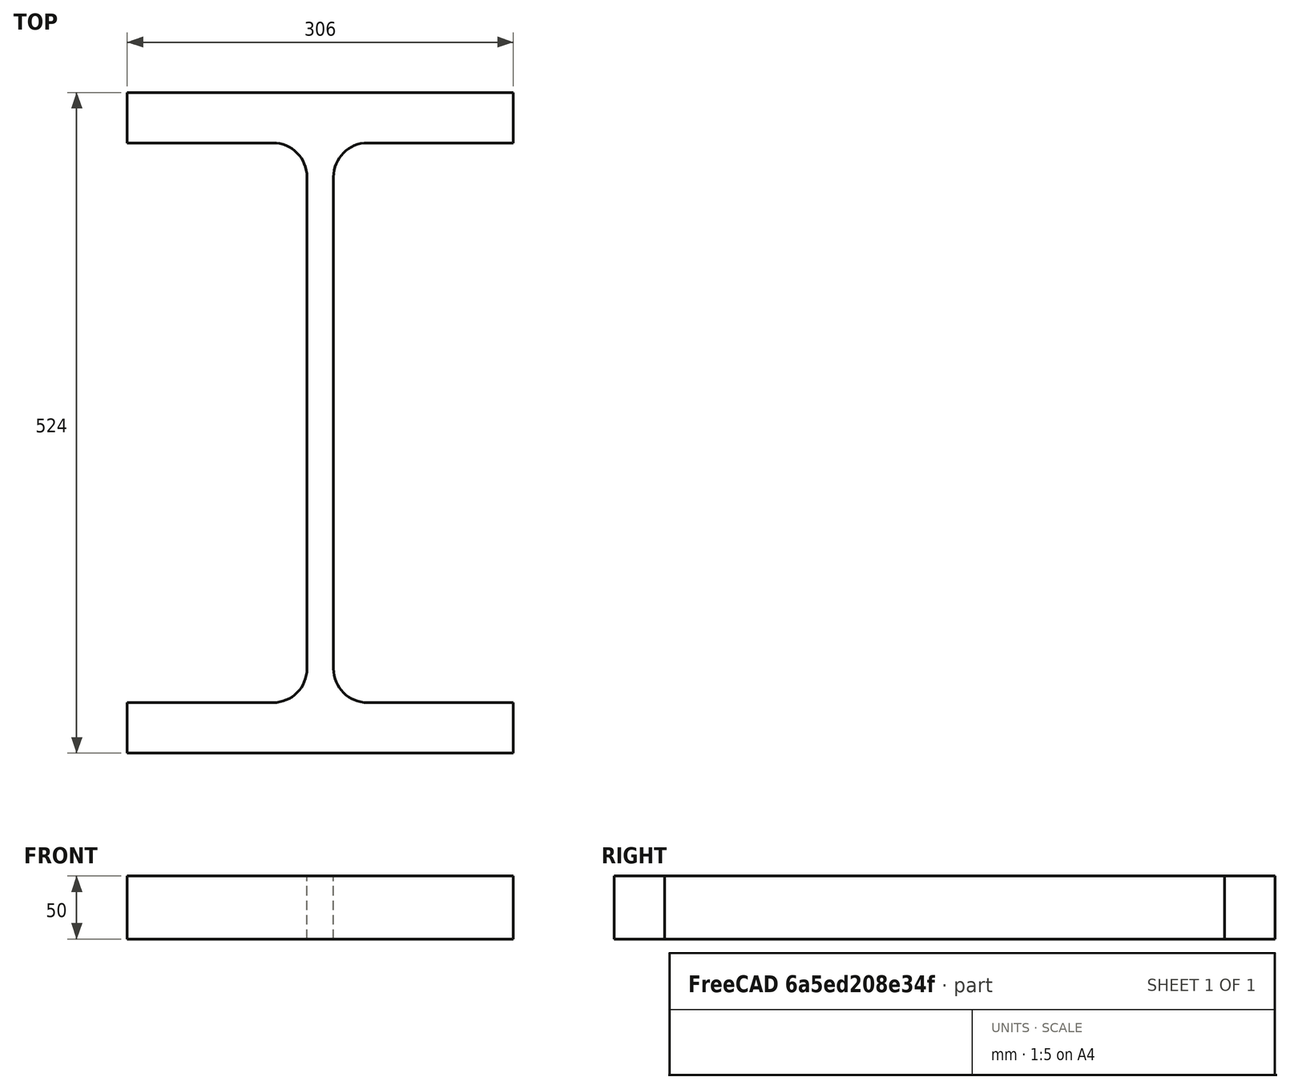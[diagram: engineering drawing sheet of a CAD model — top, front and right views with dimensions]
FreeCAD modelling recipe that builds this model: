
FCSTD DOCUMENT  (FreeCAD 0.15R4671 (Git))
Label: HE-M-Profile 500 DIN1025-4 S235JR
License: All rights reserved
LicenseURL: http://en.wikipedia.org/wiki/All_rights_reserved
objects: Sketcher::SketchObject×1, Part::Extrusion×1
note: 2 computed .brp shape members not serialized (recipe doc carries the construction recipe); baked Part::Feature solids carry a one-line shape summary decoded from their .brp

FEATURE [Sketcher::SketchObject] Sketch
  sketch-geometry (16):
    g0: LineSegment StartX=10.5 StartY=-195 StartZ=0 EndX=10.5 EndY=195 EndZ=0
    g1: LineSegment StartX=37.5 StartY=222 StartZ=0 EndX=153 EndY=222 EndZ=0
    g2: LineSegment StartX=153 StartY=222 StartZ=0 EndX=153 EndY=262 EndZ=0
    g3: LineSegment StartX=153 StartY=262 StartZ=0 EndX=-153 EndY=262 EndZ=0
    g4: LineSegment StartX=-153 StartY=262 StartZ=0 EndX=-153 EndY=222 EndZ=0
    g5: LineSegment StartX=-153 StartY=222 StartZ=0 EndX=-37.5 EndY=222 EndZ=0
    g6: LineSegment StartX=-10.5 StartY=195 StartZ=0 EndX=-10.5 EndY=-195 EndZ=0
    g7: LineSegment StartX=-37.5 StartY=-222 StartZ=0 EndX=-153 EndY=-222 EndZ=0
    g8: LineSegment StartX=-153 StartY=-222 StartZ=0 EndX=-153 EndY=-262 EndZ=0
    g9: LineSegment StartX=-153 StartY=-262 StartZ=0 EndX=153 EndY=-262 EndZ=0
    g10: LineSegment StartX=153 StartY=-262 StartZ=0 EndX=153 EndY=-222 EndZ=0
    g11: LineSegment StartX=153 StartY=-222 StartZ=0 EndX=37.5 EndY=-222 EndZ=0
    g12: ArcOfCircle CenterX=37.5 CenterY=195 CenterZ=0 NormalX=0 NormalY=0 NormalZ=1 Radius=27 StartAngle=1.5708 EndAngle=3.14159
    g13: ArcOfCircle CenterX=37.5 CenterY=-195 CenterZ=0 NormalX=0 NormalY=0 NormalZ=1 Radius=27 StartAngle=3.14159 EndAngle=4.71239
    g14: ArcOfCircle CenterX=-37.5 CenterY=195 CenterZ=0 NormalX=0 NormalY=0 NormalZ=1 Radius=27 StartAngle=0 EndAngle=1.5708
    g15: ArcOfCircle CenterX=-37.5 CenterY=-195 CenterZ=0 NormalX=0 NormalY=0 NormalZ=1 Radius=27 StartAngle=4.71239 EndAngle=6.28319
  constraints (42):
    c: Vertical(g0)
    c: Coincident(g2,g1)
    c: Vertical(g2)
    c: Coincident(g3,g2)
    c: Coincident(g4,g3)
    c: Vertical(g4)
    c: Coincident(g5,g4)
    c: Horizontal(g5)
    c: Vertical(g6)
    c: Horizontal(g7)
    c: Coincident(g8,g7)
    c: Vertical(g8)
    c: Coincident(g9,g8)
    c: Horizontal(g9)
    c: Coincident(g10,g9)
    c: Vertical(g10)
    c: Coincident(g11,g10)
    c: Horizontal(g11)
    c: Tangent(g1,g12) = 1.5708
    c: Tangent(g0,g12) = 1.5708
    c: Tangent(g0,g13) = 1.5708
    c: Tangent(g11,g13) = 1.5708
    c: Tangent(g5,g14) = 1.5708
    c: Tangent(g6,g14) = 1.5708
    c: Tangent(g6,g15) = 1.5708
    c: Tangent(g7,g15) = 1.5708
    c: Equal(g3,g9)
    c: Equal(g2,g4)
    c: Equal(g4,g8)
    c: Equal(g8,g10)
    c: Equal(g12,g14)
    c: Equal(g14,g15)
    c: Equal(g15,g13)
    c: Symmetric(g2,g3,g-2)
    c: Symmetric(g9,g8,g-2)
    c: Symmetric(g0,g6,g-2)
    c: Symmetric(g2,g9,g-1)
    c: DistanceY(g2,g9) = -524
    c: DistanceX(g3) = -306
    c: DistanceX(g0,g6) = -21
    c: DistanceY(g2) = 40
    c: Radius(g12) = 27
FEATURE [Part::Extrusion] Extrude  label="HE-M-Profile 500 DIN1025-4 S235JR"
  Base = -> Sketch
  Dir = (0,0,50)
  Solid = true
